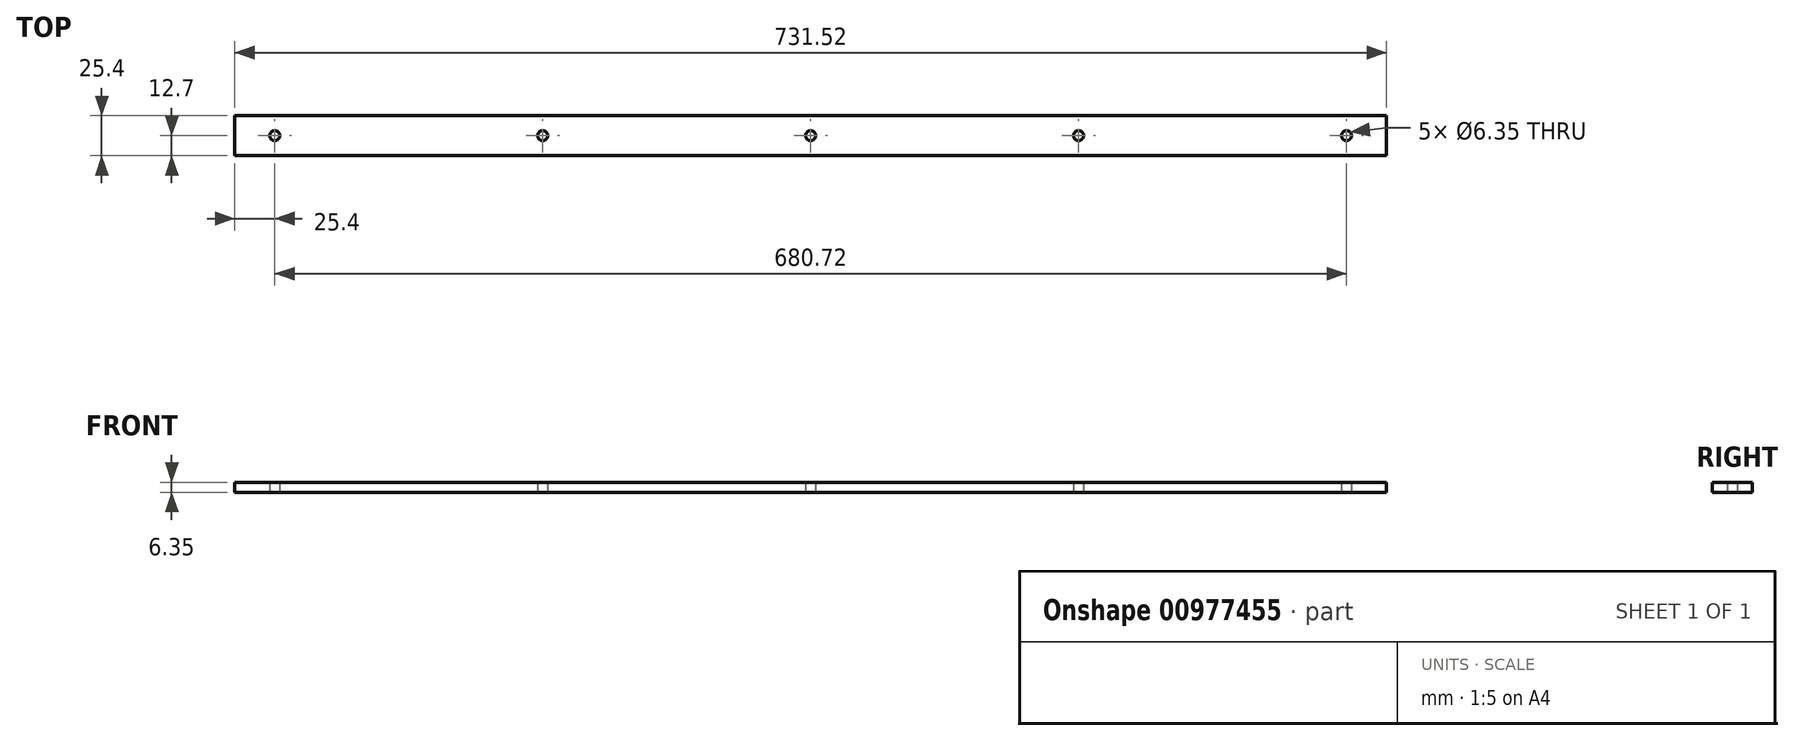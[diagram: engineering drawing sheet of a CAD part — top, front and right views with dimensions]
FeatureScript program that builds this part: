
annotation { "Feature Type Name" : "Feature", "Feature Type Description" : "" }
export const myFeature = defineFeature(function(context is Context, id is Id, definition is map)
    precondition{}
    {
        {
            var Q0;
            Q0=qCreatedBy(makeId("Top.planeOp"),FACE);
            var sketch = newSketch(context, id + "F0", { "sketchPlane" : qUnion([Q0])});
            skLineSegment(sketch, "E0.bottom", {"start": v(365.76, 12.7) * mm, "end": v(-365.76, 12.7) * mm});
            skLineSegment(sketch, "E0.top", {"start": v(365.76, -12.7) * mm, "end": v(-365.76, -12.7) * mm});
            skLineSegment(sketch, "E0.left", {"start": v(365.76, 12.7) * mm, "end": v(365.76, -12.7) * mm});
            skLineSegment(sketch, "E0.right", {"start": v(-365.76, 12.7) * mm, "end": v(-365.76, -12.7) * mm});
            skPoint(sketch, "E0.middle", {"position": v(0, 0) * mm});
            skCircle(sketch, "E1", {"center": v(0, 0) * mm, "radius": 3.18 * mm});
            skCircle(sketch, "E2", {"center": v(-170.18, 0) * mm, "radius": 3.18 * mm});
            skCircle(sketch, "E3", {"center": v(170.18, 0) * mm, "radius": 3.18 * mm});
            skCircle(sketch, "E4", {"center": v(-340.36, 0) * mm, "radius": 3.18 * mm});
            skCircle(sketch, "E5.MirrorC", {"center": v(340.36, 0) * mm, "radius": 3.18 * mm});
            skSolve(sketch);
        }
        {
            var Q0;
            Q0 = qSketchRegion(id + "F0", true);
            extrude(context, id + "F1", {"entities" : qUnion([Q0]), "depth" : 6.35 * mm, "offsetDistance" : 25.4 * mm});
        }
    });
